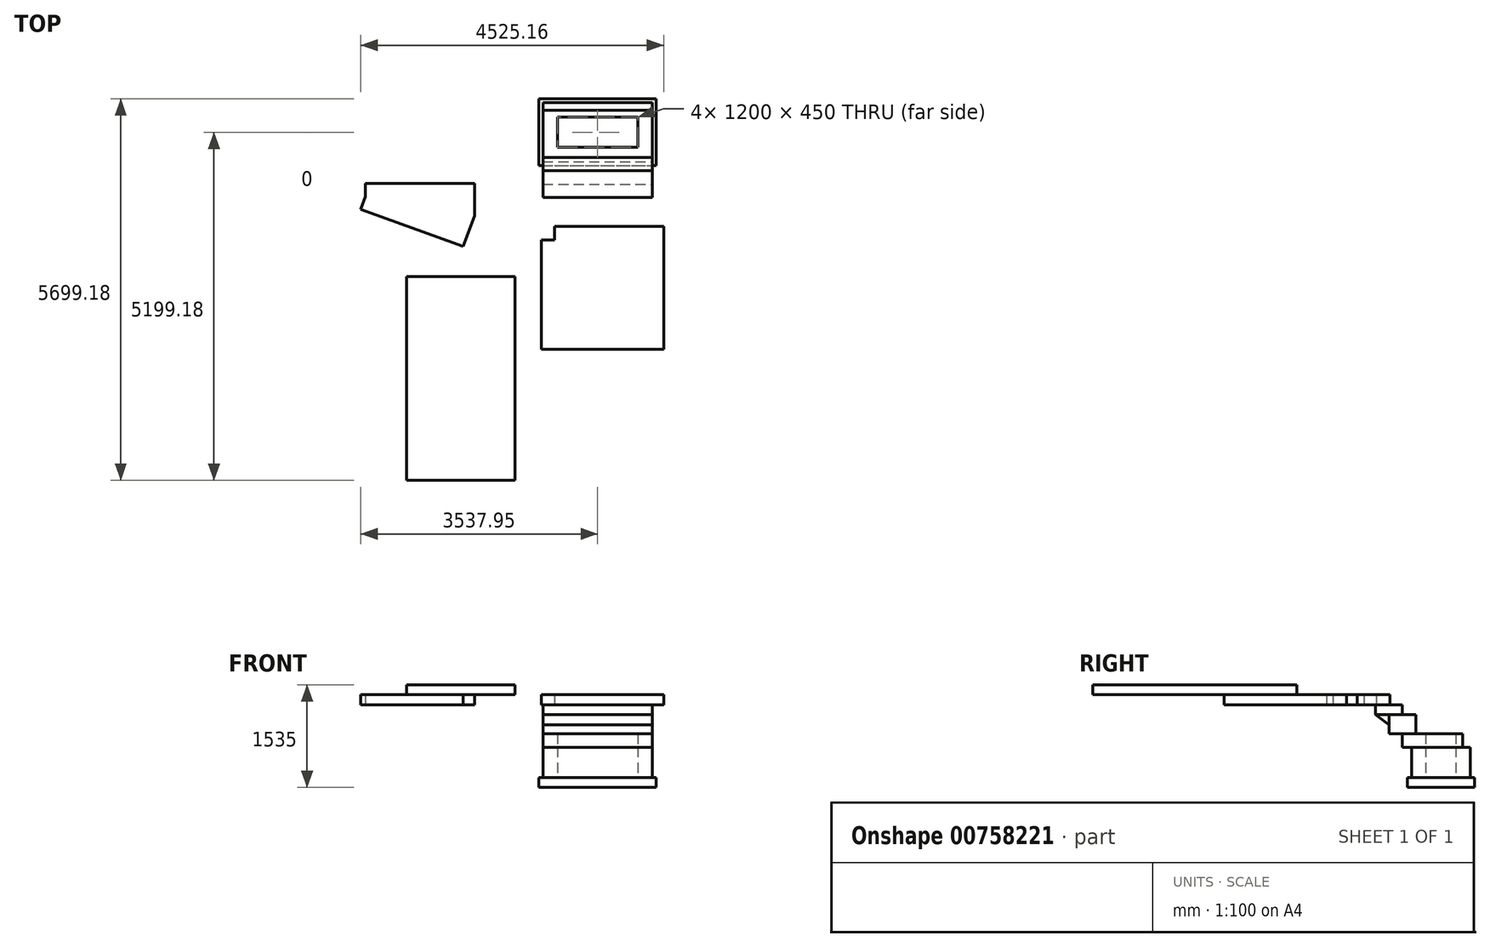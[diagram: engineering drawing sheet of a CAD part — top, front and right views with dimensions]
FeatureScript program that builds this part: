
annotation { "Feature Type Name" : "Feature", "Feature Type Description" : "" }
export const myFeature = defineFeature(function(context is Context, id is Id, definition is map)
    precondition{}
    {
        {
            var Q0;
            Q0=qCreatedBy(makeId("Top.planeOp"),FACE);
            var sketch = newSketch(context, id + "F0", { "sketchPlane" : qUnion([Q0])});
            skLineSegment(sketch, "E0", {"start": v(-102.22, -92.06) * mm, "end": v(-102.22, 907.94) * mm});
            skLineSegment(sketch, "E1", {"start": v(-102.22, 907.94) * mm, "end": v(1647.78, 907.94) * mm});
            skLineSegment(sketch, "E2", {"start": v(1647.78, 907.94) * mm, "end": v(1647.78, -92.06) * mm});
            skLineSegment(sketch, "E3", {"start": v(-102.22, -92.06) * mm, "end": v(1647.78, -92.06) * mm});
            skSolve(sketch);
        }
        {
            var Q0;
            Q0=makeQuery(id+"F0.imprint","IMPRINT",FACE,{"disambiguationData":[TD([[makeQuery(id+"F0.imprint","IMPRINT",EDGE,{"derivedFrom":sQuery(id+"F0.wireOp",EDGE,"E0")}),-1.0]])]});
            extrude(context, id + "F1", {"entities" : qUnion([Q0]), "depth" : 150 * mm, "offsetDistance" : 25 * mm});
        }
        {
            var Q0;
            Q0=makeQuery(id+"F1.opExtrude","CAP_FACE",FACE,{"disambiguationData":[OSD([sQuery(id+"F0.wireOp",EDGE,"E0"),sQuery(id+"F0.wireOp",EDGE,"E1"),sQuery(id+"F0.wireOp",EDGE,"E2"),sQuery(id+"F0.wireOp",EDGE,"E3")])],"isStart":false});
            var sketch = newSketch(context, id + "F2", { "sketchPlane" : qUnion([Q0])});
            skLineSegment(sketch, "E4.bottom", {"start": v(-42.22, -32.06) * mm, "end": v(1587.78, -32.06) * mm});
            skLineSegment(sketch, "E4.top", {"start": v(-42.22, 847.94) * mm, "end": v(1587.78, 847.94) * mm});
            skLineSegment(sketch, "E4.left", {"start": v(-42.22, -32.06) * mm, "end": v(-42.22, 847.94) * mm});
            skLineSegment(sketch, "E4.right", {"start": v(1587.78, -32.06) * mm, "end": v(1587.78, 847.94) * mm});
            skLineSegment(sketch, "E5.bottom", {"start": v(172.78, 182.94) * mm, "end": v(1372.78, 182.94) * mm});
            skLineSegment(sketch, "E5.top", {"start": v(172.78, 632.94) * mm, "end": v(1372.78, 632.94) * mm});
            skLineSegment(sketch, "E5.left", {"start": v(172.78, 182.94) * mm, "end": v(172.78, 632.94) * mm});
            skLineSegment(sketch, "E5.right", {"start": v(1372.78, 182.94) * mm, "end": v(1372.78, 632.94) * mm});
            skSolve(sketch);
        }
        {
            var Q0;
            Q0=makeQuery(id+"F2.imprint","IMPRINT",FACE,{"disambiguationData":[TD([[makeQuery(id+"F2.imprint","IMPRINT",EDGE,{"derivedFrom":sQuery(id+"F2.wireOp",EDGE,"E4.bottom")}),1.0]])]});
            extrude(context, id + "F3", {"entities" : qUnion([Q0]), "depth" : 450 * mm, "offsetDistance" : 25 * mm});
        }
        {
            var Q0;
            Q0=makeQuery(id+"F3.opExtrude","CAP_FACE",FACE,{"disambiguationData":[OSD([sQuery(id+"F2.wireOp",EDGE,"E4.bottom"),sQuery(id+"F2.wireOp",EDGE,"E4.top"),sQuery(id+"F2.wireOp",EDGE,"E4.left"),sQuery(id+"F2.wireOp",EDGE,"E4.right"),sQuery(id+"F2.wireOp",EDGE,"E5.bottom"),sQuery(id+"F2.wireOp",EDGE,"E5.top"),sQuery(id+"F2.wireOp",EDGE,"E5.left"),sQuery(id+"F2.wireOp",EDGE,"E5.right")])],"isStart":false});
            var sketch = newSketch(context, id + "F4", { "sketchPlane" : qUnion([Q0])});
            skLineSegment(sketch, "E6.bottom", {"start": v(172.78, 182.94) * mm, "end": v(1372.78, 182.94) * mm});
            skLineSegment(sketch, "E6.top", {"start": v(172.78, 632.94) * mm, "end": v(1372.78, 632.94) * mm});
            skLineSegment(sketch, "E6.left", {"start": v(172.78, 182.94) * mm, "end": v(172.78, 632.94) * mm});
            skLineSegment(sketch, "E6.right", {"start": v(1372.78, 182.94) * mm, "end": v(1372.78, 632.94) * mm});
            skLineSegment(sketch, "E7.bottom", {"start": v(-42.22, -167.06) * mm, "end": v(1587.78, -167.06) * mm});
            skLineSegment(sketch, "E7.top", {"start": v(-42.22, 732.94) * mm, "end": v(1587.78, 732.94) * mm});
            skLineSegment(sketch, "E7.left", {"start": v(-42.22, -167.06) * mm, "end": v(-42.22, 732.94) * mm});
            skLineSegment(sketch, "E7.right", {"start": v(1587.78, -167.06) * mm, "end": v(1587.78, 732.94) * mm});
            skSolve(sketch);
        }
        {
            var Q0;
            Q0=makeQuery(id+"F4.imprint","IMPRINT",FACE,{"disambiguationData":[TD([[makeQuery(id+"F4.imprint","IMPRINT",EDGE,{"derivedFrom":sQuery(id+"F4.wireOp",EDGE,"E7.bottom")}),1.0]])]});
            var Q1;
            Q1=makeQuery(id+"F4.imprint","IMPRINT",FACE,{"disambiguationData":[TD([[makeQuery(id+"F4.imprint","IMPRINT",EDGE,{"derivedFrom":sQuery(id+"F4.wireOp",EDGE,"E6.bottom")}),-1.0]])]});
            extrude(context, id + "F5", {"entities" : qUnion([Q0, Q1]), "depth" : 200 * mm, "offsetDistance" : 25 * mm});
        }
        {
            var Q0;
            Q0=makeQuery(id+"F5.opExtrude","CAP_FACE",FACE,{"disambiguationData":[OSD([sQuery(id+"F4.wireOp",EDGE,"E6.bottom"),sQuery(id+"F4.wireOp",EDGE,"E6.top"),sQuery(id+"F4.wireOp",EDGE,"E6.left"),sQuery(id+"F4.wireOp",EDGE,"E6.right"),sQuery(id+"F4.wireOp",EDGE,"E7.bottom"),sQuery(id+"F4.wireOp",EDGE,"E7.top"),sQuery(id+"F4.wireOp",EDGE,"E7.left"),sQuery(id+"F4.wireOp",EDGE,"E7.right")])],"isStart":false});
            var sketch = newSketch(context, id + "F6", { "sketchPlane" : qUnion([Q0])});
            skLineSegment(sketch, "E8.bottom", {"start": v(-42.22, 32.94) * mm, "end": v(1587.78, 32.94) * mm});
            skLineSegment(sketch, "E8.top", {"start": v(-42.22, -367.06) * mm, "end": v(1587.78, -367.06) * mm});
            skLineSegment(sketch, "E9", {"start": v(1587.78, 32.94) * mm, "end": v(1587.78, -367.06) * mm});
            skLineSegment(sketch, "E10", {"start": v(-42.22, 32.94) * mm, "end": v(-42.22, -367.06) * mm});
            skSolve(sketch);
        }
        {
            var Q0;
            {var subQ0=sQuery(id+"F6.wireOp",EDGE,"E8.top");Q0=makeQuery(id+"F6.imprint","IMPRINT",FACE,{"disambiguationData":[TD([[makeQuery(id+"F6.imprint","IMPRINT",EDGE,{"derivedFrom":subQ0}),1.0]])]});}
            var Q1;
            {var subQ0=sQuery(id+"F6.wireOp",EDGE,"E8.bottom");Q1=makeQuery(id+"F6.imprint","IMPRINT",FACE,{"disambiguationData":[TD([[makeQuery(id+"F6.imprint","IMPRINT",EDGE,{"derivedFrom":subQ0}),-1.0]])]});}
            extrude(context, id + "F7", {"entities" : qUnion([Q0, Q1]), "depth" : 285 * mm, "offsetDistance" : 25 * mm});
        }
        {
            var Q0;
            Q0=makeQuery(id+"F7.opExtrude","CAP_FACE",FACE,{"disambiguationData":[OSD([sQuery(id+"F6.wireOp",EDGE,"E8.bottom"),sQuery(id+"F6.wireOp",EDGE,"E8.top"),sQuery(id+"F6.wireOp",EDGE,"E8.left"),sQuery(id+"F6.wireOp",EDGE,"E8.right")])],"isStart":false});
            var sketch = newSketch(context, id + "F8", { "sketchPlane" : qUnion([Q0])});
            skLineSegment(sketch, "E11.right", {"start": v(-42.22, -167.06) * mm, "end": v(-42.22, -567.06) * mm});
            skLineSegment(sketch, "E12", {"start": v(-42.22, -567.06) * mm, "end": v(1587.78, -567.06) * mm});
            skLineSegment(sketch, "E13", {"start": v(1587.78, -567.06) * mm, "end": v(1587.78, -167.06) * mm});
            skLineSegment(sketch, "E14", {"start": v(1587.78, -167.06) * mm, "end": v(-42.22, -167.06) * mm});
            skSolve(sketch);
        }
        {
            var Q0;
            {var subQ2=sQuery(id+"F8.wireOp",EDGE,"E12");Q0=makeQuery(id+"F8.imprint","IMPRINT",FACE,{"disambiguationData":[TD([[makeQuery(id+"F8.imprint","IMPRINT",EDGE,{"derivedFrom":subQ2}),1.0]])]});}
            var Q1;
            {var subQ2=sQuery(id+"F8.wireOp",EDGE,"E14");Q1=makeQuery(id+"F8.imprint","IMPRINT",FACE,{"disambiguationData":[TD([[makeQuery(id+"F8.imprint","IMPRINT",EDGE,{"derivedFrom":subQ2}),1.0]])]});}
            extrude(context, id + "F9", {"entities" : qUnion([Q0, Q1]), "depth" : 150 * mm, "offsetDistance" : 25 * mm});
        }
        {
            var Q0;
            Q0=makeQuery(id+"F9.opExtrude","SWEPT_FACE",FACE,{"disambiguationData":[OSD([sQuery(id+"F8.wireOp",EDGE,"E13")])]});
            var sketch = newSketch(context, id + "F10", { "sketchPlane" : qUnion([Q0])});
            skLineSegment(sketch, "E15.0", {"start": v(-367.06, 1085) * mm, "end": v(-367.06, 935) * mm});
            skLineSegment(sketch, "E16.0", {"start": v(-567.06, 1085) * mm, "end": v(-367.06, 1085) * mm});
            skLineSegment(sketch, "E17", {"start": v(-567.06, 1085) * mm, "end": v(-367.06, 935) * mm});
            skPoint(sketch, "E18.orphan", {"position": v(-367.06, 800) * mm});
            skPoint(sketch, "E19.orphan", {"position": v(-167.06, 1085) * mm});
            skSolve(sketch);
        }
        {
            var Q0;
            Q0=makeQuery(id+"F10.imprint","IMPRINT",FACE,{"disambiguationData":[TD([[makeQuery(id+"F10.imprint","IMPRINT",EDGE,{"derivedFrom":sQuery(id+"F10.wireOp",EDGE,"E15.0")}),-1.0]])]});
            extrude(context, id + "F11", {"entities" : qUnion([Q0]), "oppositeDirection" : true, "depth" : 1630 * mm, "offsetDistance" : 25 * mm});
        }
        {
            var Q0;
            Q0=makeQuery(id+"F9.opExtrude","CAP_FACE",FACE,{"disambiguationData":[OSD([sQuery(id+"F8.wireOp",EDGE,"E11.right"),sQuery(id+"F8.wireOp",EDGE,"E12"),sQuery(id+"F8.wireOp",EDGE,"E13"),sQuery(id+"F8.wireOp",EDGE,"E14")])],"isStart":false});
            var sketch = newSketch(context, id + "F12", { "sketchPlane" : qUnion([Q0])});
            skLineSegment(sketch, "E20", {"start": v(129.99, -1001.66) * mm, "end": v(1759.99, -1001.66) * mm});
            skLineSegment(sketch, "E21", {"start": v(1759.99, -1001.66) * mm, "end": v(1759.99, -2831.66) * mm});
            skLineSegment(sketch, "E22", {"start": v(1759.99, -2831.66) * mm, "end": v(-70.01, -2831.66) * mm});
            skLineSegment(sketch, "E23", {"start": v(-70.01, -2831.66) * mm, "end": v(-70.01, -1201.66) * mm});
            skLineSegment(sketch, "E24", {"start": v(-70.01, -1201.66) * mm, "end": v(129.99, -1201.66) * mm});
            skLineSegment(sketch, "E25", {"start": v(129.99, -1201.66) * mm, "end": v(129.99, -1001.66) * mm});
            skSolve(sketch);
        }
        {
            var Q0;
            Q0=makeQuery(id+"F12.imprint","IMPRINT",FACE,{"disambiguationData":[TD([[makeQuery(id+"F12.imprint","IMPRINT",EDGE,{"derivedFrom":sQuery(id+"F12.wireOp",EDGE,"E20")}),-1.0]])]});
            extrude(context, id + "F13", {"entities" : qUnion([Q0]), "depth" : 150 * mm, "offsetDistance" : 25 * mm});
        }
        {
            var Q0;
            Q0=makeQuery(id+"F13.opExtrude","CAP_FACE",FACE,{"disambiguationData":[OSD([sQuery(id+"F12.wireOp",EDGE,"E20"),sQuery(id+"F12.wireOp",EDGE,"E21"),sQuery(id+"F12.wireOp",EDGE,"E22"),sQuery(id+"F12.wireOp",EDGE,"E23"),sQuery(id+"F12.wireOp",EDGE,"E24"),sQuery(id+"F12.wireOp",EDGE,"E25")])],"isStart":false});
            var sketch = newSketch(context, id + "F14", { "sketchPlane" : qUnion([Q0])});
            skLineSegment(sketch, "E26.bottom", {"start": v(-463.78, -1746.24) * mm, "end": v(-2078.78, -1746.24) * mm});
            skLineSegment(sketch, "E26.top", {"start": v(-463.78, -4791.24) * mm, "end": v(-2078.78, -4791.24) * mm});
            skLineSegment(sketch, "E26.left", {"start": v(-463.78, -1746.24) * mm, "end": v(-463.78, -4791.24) * mm});
            skLineSegment(sketch, "E26.right", {"start": v(-2078.78, -1746.24) * mm, "end": v(-2078.78, -4791.24) * mm});
            skSolve(sketch);
        }
        {
            var Q0;
            Q0=makeQuery(id+"F14.imprint","IMPRINT",FACE,{"disambiguationData":[TD([[makeQuery(id+"F14.imprint","IMPRINT",EDGE,{"derivedFrom":sQuery(id+"F14.wireOp",EDGE,"E26.bottom")}),1.0]])]});
            extrude(context, id + "F15", {"entities" : qUnion([Q0]), "depth" : 150 * mm, "offsetDistance" : 25 * mm});
        }
        {
            var Q0;
            Q0=makeQuery(id+"F9.opExtrude","CAP_FACE",FACE,{"disambiguationData":[OSD([sQuery(id+"F8.wireOp",EDGE,"E11.right"),sQuery(id+"F8.wireOp",EDGE,"E12"),sQuery(id+"F8.wireOp",EDGE,"E13"),sQuery(id+"F8.wireOp",EDGE,"E14")])],"isStart":false});
            var sketch = newSketch(context, id + "F16", { "sketchPlane" : qUnion([Q0])});
            skLineSegment(sketch, "E27", {"start": v(-1066.77, -354.23) * mm, "end": v(-2696.77, -354.23) * mm});
            skLineSegment(sketch, "E28", {"start": v(-2696.77, -354.23) * mm, "end": v(-2696.77, -554.23) * mm});
            skLineSegment(sketch, "E29", {"start": v(-2696.77, -554.23) * mm, "end": v(-2765.17, -742.17) * mm});
            skLineSegment(sketch, "E30", {"start": v(-2765.17, -742.17) * mm, "end": v(-1233.47, -1299.66) * mm});
            skLineSegment(sketch, "E31", {"start": v(-1233.47, -1299.66) * mm, "end": v(-1066.77, -841.64) * mm});
            skLineSegment(sketch, "E32", {"start": v(-1066.77, -354.23) * mm, "end": v(-1066.77, -841.64) * mm});
            skSolve(sketch);
        }
        {
            var Q0;
            Q0=makeQuery(id+"F16.imprint","IMPRINT",FACE,{"disambiguationData":[TD([[makeQuery(id+"F16.imprint","IMPRINT",EDGE,{"derivedFrom":sQuery(id+"F16.wireOp",EDGE,"E27")}),1.0]])]});
            extrude(context, id + "F17", {"entities" : qUnion([Q0]), "depth" : 150 * mm, "offsetDistance" : 25 * mm});
        }
    });
